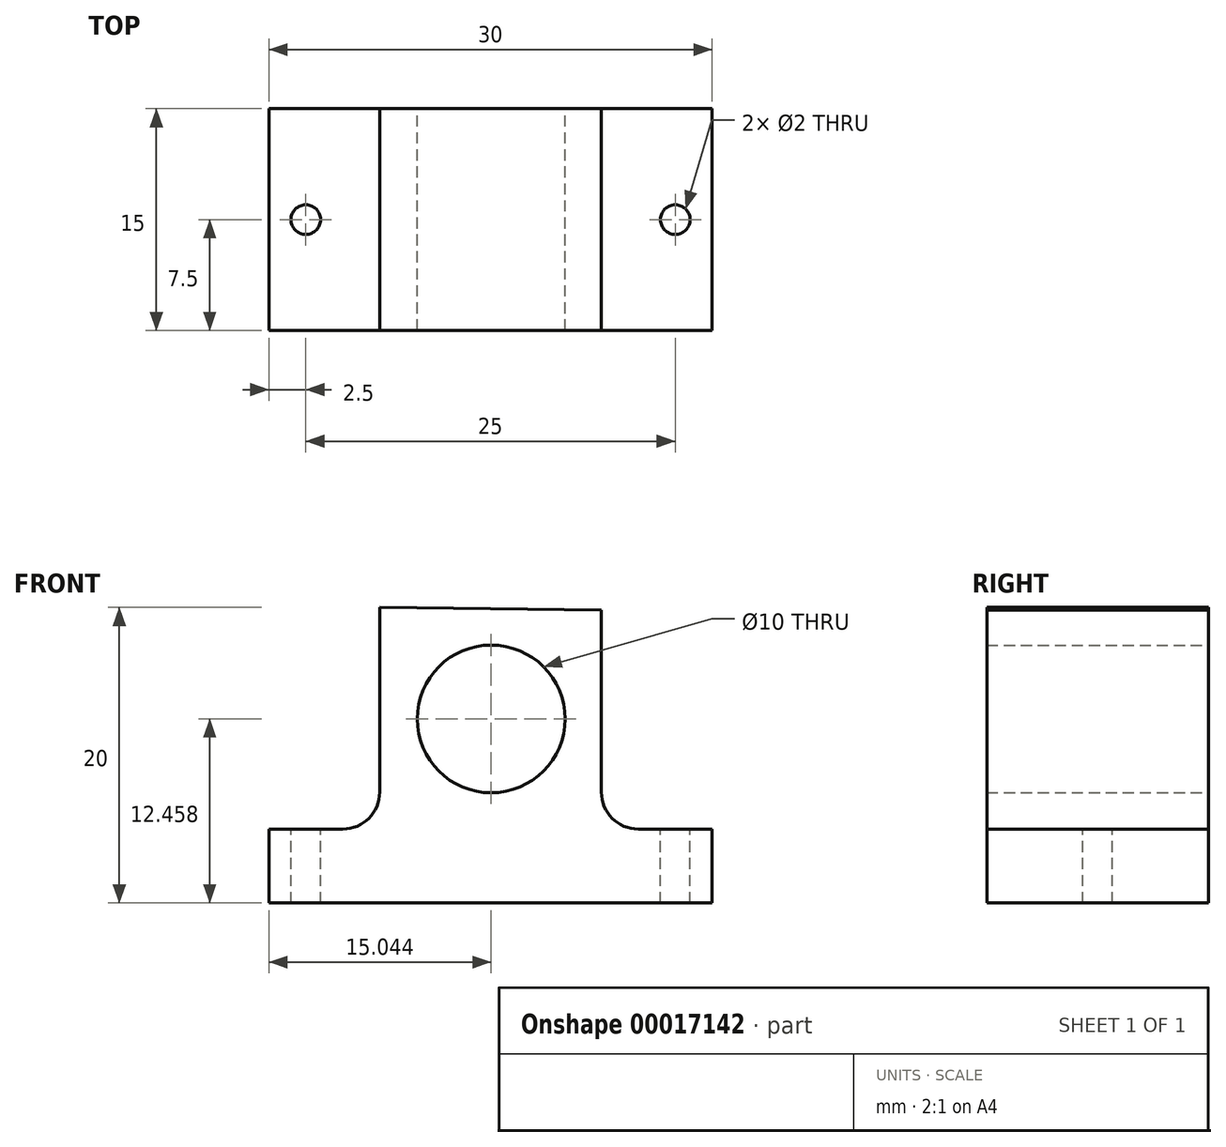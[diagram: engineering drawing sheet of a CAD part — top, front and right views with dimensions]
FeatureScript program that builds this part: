
annotation { "Feature Type Name" : "Feature", "Feature Type Description" : "" }
export const myFeature = defineFeature(function(context is Context, id is Id, definition is map)
    precondition{}
    {
        {
            var Q0;
            Q0=qCreatedBy(makeId("Front.planeOp"),FACE);
            var sketch = newSketch(context, id + "F0", { "sketchPlane" : qUnion([Q0])});
            skLineSegment(sketch, "E0", {"start": v(-7.5, -22.62) * mm, "end": v(22.5, -22.62) * mm});
            skLineSegment(sketch, "E1", {"start": v(22.5, -22.62) * mm, "end": v(22.5, -17.62) * mm});
            skLineSegment(sketch, "E2", {"start": v(-7.5, -22.62) * mm, "end": v(-7.5, -17.62) * mm});
            skLineSegment(sketch, "E3", {"start": v(-7.5, -17.62) * mm, "end": v(-2.5, -17.62) * mm});
            skLineSegment(sketch, "E4", {"start": v(22.5, -17.62) * mm, "end": v(17.5, -17.62) * mm});
            skLineSegment(sketch, "E5", {"start": v(0, -15.12) * mm, "end": v(0, -2.62) * mm});
            skLineSegment(sketch, "E6", {"start": v(15, -15.12) * mm, "end": v(15, -2.8) * mm});
            skLineSegment(sketch, "E7", {"start": v(0, -2.62) * mm, "end": v(15, -2.8) * mm});
            skPoint(sketch, "E8.visualSharp", {"position": v(0, -17.62) * mm});
            skArc(sketch, "E8.filletArc", {"start": v(-2.5, -17.62) * mm, "mid": v(-0.73, -16.89) * mm, "end": v(0, -15.12) * mm});
            skPoint(sketch, "E9.visualSharp", {"position": v(15, -17.62) * mm});
            skArc(sketch, "E9.filletArc", {"start": v(15, -15.12) * mm, "mid": v(15.73, -16.89) * mm, "end": v(17.5, -17.62) * mm});
            skCircle(sketch, "E10", {"center": v(7.54, -10.16) * mm, "radius": 5 * mm});
            skSolve(sketch);
        }
        {
            var Q0;
            Q0 = qSketchRegion(id + "F0", true);
            extrude(context, id + "F1", {"entities" : qUnion([Q0]), "depth" : 15 * mm});
        }
        {
            var Q0;
            Q0=makeQuery(id+"F1.opExtrude","SWEPT_FACE",FACE,{"disambiguationData":[OSD([sQuery(id+"F0.wireOp",EDGE,"E3")])]});
            var sketch = newSketch(context, id + "F2", { "sketchPlane" : qUnion([Q0])});
            skCircle(sketch, "E11", {"center": v(-5, -7.5) * mm, "radius": 1 * mm});
            skSolve(sketch);
        }
        {
            var Q0;
            Q0=makeQuery(id+"F1.opExtrude","SWEPT_FACE",FACE,{"disambiguationData":[OSD([sQuery(id+"F0.wireOp",EDGE,"E4")])]});
            var sketch = newSketch(context, id + "F3", { "sketchPlane" : qUnion([Q0])});
            skCircle(sketch, "E12", {"center": v(20, -7.5) * mm, "radius": 1 * mm});
            skSolve(sketch);
        }
        {
            var Q0;
            Q0=makeQuery(id+"F3.imprint","IMPRINT",FACE,{"disambiguationData":[TD([[makeQuery(id+"F3.imprint","IMPRINT",EDGE,{"derivedFrom":sQuery(id+"F3.wireOp",EDGE,"E12")}),-1.0]])]});
            var sketch = newSketch(context, id + "F4", { "sketchPlane" : qUnion([Q0])});
            skSolve(sketch);
        }
        {
            var Q0;
            Q0 = qSketchRegion(id + "F4", true);
            var Q1;
            Q1=makeQuery(id+"F3.imprint","IMPRINT",FACE,{"disambiguationData":[TD([[makeQuery(id+"F3.imprint","IMPRINT",EDGE,{"derivedFrom":sQuery(id+"F3.wireOp",EDGE,"E12")}),1.0]])]});
            var Q2;
            Q2=makeQuery(id+"F2.imprint","IMPRINT",FACE,{"disambiguationData":[TD([[makeQuery(id+"F2.imprint","IMPRINT",EDGE,{"derivedFrom":sQuery(id+"F2.wireOp",EDGE,"E11")}),1.0]])]});
            extrude(context, id + "F5", {"entities" : qUnion([Q0, Q1, Q2]), "operationType" : NewBodyOperationType.REMOVE, "endBound" : BoundingType.THROUGH_ALL, "oppositeDirection" : true, "depth" : 25 * mm});
        }
    });
